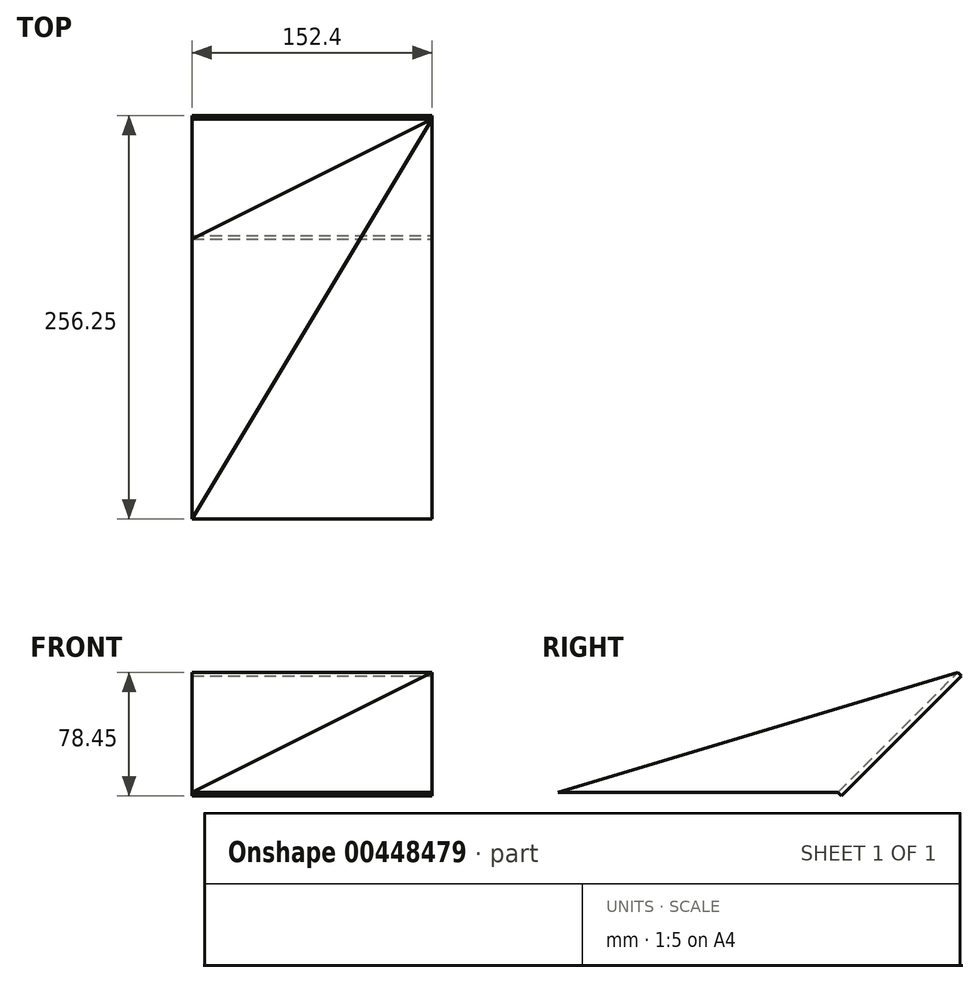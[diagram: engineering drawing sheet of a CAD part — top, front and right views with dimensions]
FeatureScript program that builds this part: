
annotation { "Feature Type Name" : "Feature", "Feature Type Description" : "" }
export const myFeature = defineFeature(function(context is Context, id is Id, definition is map)
    precondition{}
    {
        {
            var Q0;
            Q0=qCreatedBy(makeId("Top.planeOp"),FACE);
            var sketch = newSketch(context, id + "F0", { "sketchPlane" : qUnion([Q0])});
            skLineSegment(sketch, "E0.bottom", {"start": v(0, 0) * mm, "end": v(152.4, 0) * mm});
            skLineSegment(sketch, "E0.top", {"start": v(0, 254) * mm, "end": v(152.4, 254) * mm});
            skLineSegment(sketch, "E0.left", {"start": v(0, 0) * mm, "end": v(0, 254) * mm});
            skLineSegment(sketch, "E0.right", {"start": v(152.4, 0) * mm, "end": v(152.4, 254) * mm});
            skSolve(sketch);
        }
        {
            var Q0;
            Q0=makeQuery(id+"F0.imprint","IMPRINT",FACE,{"disambiguationData":[TD([[makeQuery(id+"F0.imprint","IMPRINT",EDGE,{"derivedFrom":sQuery(id+"F0.wireOp",EDGE,"E0.bottom")}),1.0]])]});
            extrude(context, id + "F1", {"entities" : qUnion([Q0]), "depth" : 76.2 * mm});
        }
        {
            var Q0;
            Q0=makeQuery(id+"F1.opExtrude","SWEPT_FACE",FACE,{"disambiguationData":[OSD([sQuery(id+"F0.wireOp",EDGE,"E0.right")])]});
            var sketch = newSketch(context, id + "F2", { "sketchPlane" : qUnion([Q0])});
            skLineSegment(sketch, "E1", {"start": v(0, 0) * mm, "end": v(254, 76.2) * mm});
            skLineSegment(sketch, "E2", {"start": v(254, 76.2) * mm, "end": v(0, 76.2) * mm});
            skLineSegment(sketch, "E3", {"start": v(0, 76.2) * mm, "end": v(0, 0) * mm});
            skSolve(sketch);
        }
        {
            var Q0;
            Q0=makeQuery(id+"F2.imprint","IMPRINT",FACE,{"disambiguationData":[TD([[makeQuery(id+"F2.imprint","IMPRINT",EDGE,{"derivedFrom":sQuery(id+"F2.wireOp",EDGE,"E1")}),1.0]])]});
            extrude(context, id + "F3", {"entities" : qUnion([Q0]), "operationType" : NewBodyOperationType.REMOVE, "endBound" : BoundingType.UP_TO_NEXT, "oppositeDirection" : true, "depth" : 25.4 * mm});
        }
        {
            var Q0;
            Q0=makeQuery(id+"F1.opExtrude","SWEPT_FACE",FACE,{"disambiguationData":[OSD([sQuery(id+"F0.wireOp",EDGE,"E0.top")])]});
            var sketch = newSketch(context, id + "F4", { "sketchPlane" : qUnion([Q0])});
            skLineSegment(sketch, "E4", {"start": v(-152.4, 76.2) * mm, "end": v(0, 0) * mm});
            skLineSegment(sketch, "E5", {"start": v(0, 0) * mm, "end": v(0, 76.2) * mm});
            skLineSegment(sketch, "E6", {"start": v(0, 76.2) * mm, "end": v(-152.4, 76.2) * mm});
            skSolve(sketch);
        }
        {
            var Q0;
            Q0=makeQuery(id+"F4.imprint","IMPRINT",FACE,{"disambiguationData":[TD([[makeQuery(id+"F4.imprint","IMPRINT",EDGE,{"derivedFrom":sQuery(id+"F4.wireOp",EDGE,"E4")}),1.0]])]});
            extrude(context, id + "F5", {"entities" : qUnion([Q0]), "operationType" : NewBodyOperationType.REMOVE, "endBound" : BoundingType.UP_TO_NEXT, "oppositeDirection" : true, "depth" : 25.4 * mm});
        }
        {
            var Q0;
            Q0=makeQuery(id+"F1.opExtrude","SWEPT_FACE",FACE,{"disambiguationData":[OSD([sQuery(id+"F0.wireOp",EDGE,"E0.right")])]});
            var sketch = newSketch(context, id + "F6", { "sketchPlane" : qUnion([Q0])});
            skLineSegment(sketch, "E7", {"start": v(254, 76.2) * mm, "end": v(177.8, 0) * mm});
            skLineSegment(sketch, "E8", {"start": v(177.8, 0) * mm, "end": v(254, 0) * mm});
            skLineSegment(sketch, "E9", {"start": v(254, 0) * mm, "end": v(254, 76.2) * mm});
            skSolve(sketch);
        }
        {
            var Q0;
            Q0=makeQuery(id+"F6.imprint","IMPRINT",FACE,{"disambiguationData":[TD([[makeQuery(id+"F6.imprint","IMPRINT",EDGE,{"derivedFrom":sQuery(id+"F6.wireOp",EDGE,"E7")}),1.0]])]});
            extrude(context, id + "F7", {"entities" : qUnion([Q0]), "operationType" : NewBodyOperationType.REMOVE, "endBound" : BoundingType.UP_TO_NEXT, "oppositeDirection" : true, "depth" : 25.4 * mm});
        }
        {
            var Q0;
            Q0=makeQuery(id+"F7.boolean.opBoolean","COPY",FACE,{"derivedFrom":makeQuery(id+"F7.opExtrude","SWEPT_FACE",FACE,{"disambiguationData":[OSD([sQuery(id+"F6.wireOp",EDGE,"E7")])]})});
            var sketch = newSketch(context, id + "F8", { "sketchPlane" : qUnion([Q0])});
            skLineSegment(sketch, "E10.bottom", {"start": v(0, 125.72) * mm, "end": v(-152.4, 125.72) * mm});
            skLineSegment(sketch, "E10.top", {"start": v(0, 233.49) * mm, "end": v(-152.4, 233.49) * mm});
            skLineSegment(sketch, "E10.left", {"start": v(0, 125.72) * mm, "end": v(0, 233.49) * mm});
            skLineSegment(sketch, "E10.right", {"start": v(-152.4, 125.72) * mm, "end": v(-152.4, 233.49) * mm});
            skSolve(sketch);
        }
        {
            var Q0;
            Q0=makeQuery(id+"F8.imprint","IMPRINT",FACE,{"disambiguationData":[TD([[makeQuery(id+"F8.imprint","IMPRINT",EDGE,{"derivedFrom":sQuery(id+"F8.wireOp",EDGE,"E10.top")}),1.0]])]});
            var Q1;
            Q1=makeQuery(id+"F8.imprint","IMPRINT",FACE,{"disambiguationData":[TD([[makeQuery(id+"F8.imprint","IMPRINT",EDGE,{"derivedFrom":sQuery(id+"F8.wireOp",EDGE,"E10.bottom")}),-1.0]])]});
            extrude(context, id + "F9", {"entities" : qUnion([Q0, Q1]), "operationType" : NewBodyOperationType.ADD, "depth" : 3.17 * mm});
        }
    });
